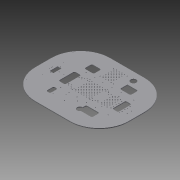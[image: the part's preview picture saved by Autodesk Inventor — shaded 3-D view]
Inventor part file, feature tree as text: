
AUTODESK INVENTOR PART (.ipt)
format: ipt  version: 2013 (Build 170138000, 138)  size: 545,792 bytes
history: native  units: mm
features: extrude x1, sketch x1
ambient origin geometry x8: Origin, YZ Plane, XZ Plane, XY Plane, X Axis, Y Axis, Z Axis, Center Point
bodies: Solid1 (feature_tree)
feature tree (2):
  extrude  "Extrusion1"  Depth=3.0mm
  sketch  "Sketch1"  dims[d51=3.0mm d54=3.0mm d64=3.0mm d69=3.0mm d76=3.0mm d77=3.0mm d78=51.0mm d82=51.0mm d90=22.0mm d91=25.0mm d92=5.0mm d94=51.0mm d96=51.0mm d116=64.0mm d117=3.0mm d118=3.0mm d119=3.0mm d120=3.0mm d121=3.0mm d122=5.632993mm d125=4.7mm d126=5.0mm d128=10.0mm d129=5.0mm d130=10.0mm d131=5.0mm d132=66.0mm d134=3.0mm d135=3.0mm d137=3.0mm d138=5.682993mm d139=4.7mm d140=5.0mm d141=10.0mm d142=5.0mm d143=3.0mm d144=5.0mm d145=5.0mm d150=3.0mm d153=3.0mm d160=36.2mm d162=50.0mm d163=5.0mm d164=40.0mm d165=28.5mm d166=5.0mm d170=5.0mm d171=35.0mm d172=5.0mm d177=66.0mm d182=15.0mm d184=3.0mm d185=10.0mm d186=25.0mm d187=3.0mm d188=25.0mm d189=10.0mm d190=3.0mm d196=3.0mm d197=3.0mm d198=30.0mm d199=60.0mm d200=10.0mm d201=35.0mm d202=3.0mm d203=30.0mm d204=34.23504mm d205=34.23504mm d206=35.0mm d207=30.0mm d208=31.5mm d209=31.5mm d210=50.55mm d212=5.554212mm d213=5.554212mm d214=5.0mm d215=5.0mm d216=5.554212mm d217=5.117007mm d219=5.0mm d220=5.0mm d221=5.117007mm d224=3.0mm d230=21.0mm d232=14.0mm d233=7.0mm d236=2.0mm d238=13.0mm d239=3.0mm d240=22.0mm d243=22.0mm d244=3.0mm d245=26.4mm d246=22.0mm d247=8.0mm d248=3.0mm d249=3.0mm d250=26.4mm d251=22.0mm d252=16.0mm d264=3.0mm d265=3.0mm d267=10.0mm d268=20.0mm d269=3.0mm d270=10.0mm d272=175.0mm d273=140.0mm d274=280.0mm d279=5.0mm d281=21.0mm d282=40.0mm d283=0.0mm d291=2.0mm d292=3.0mm d293=0.0mm]
